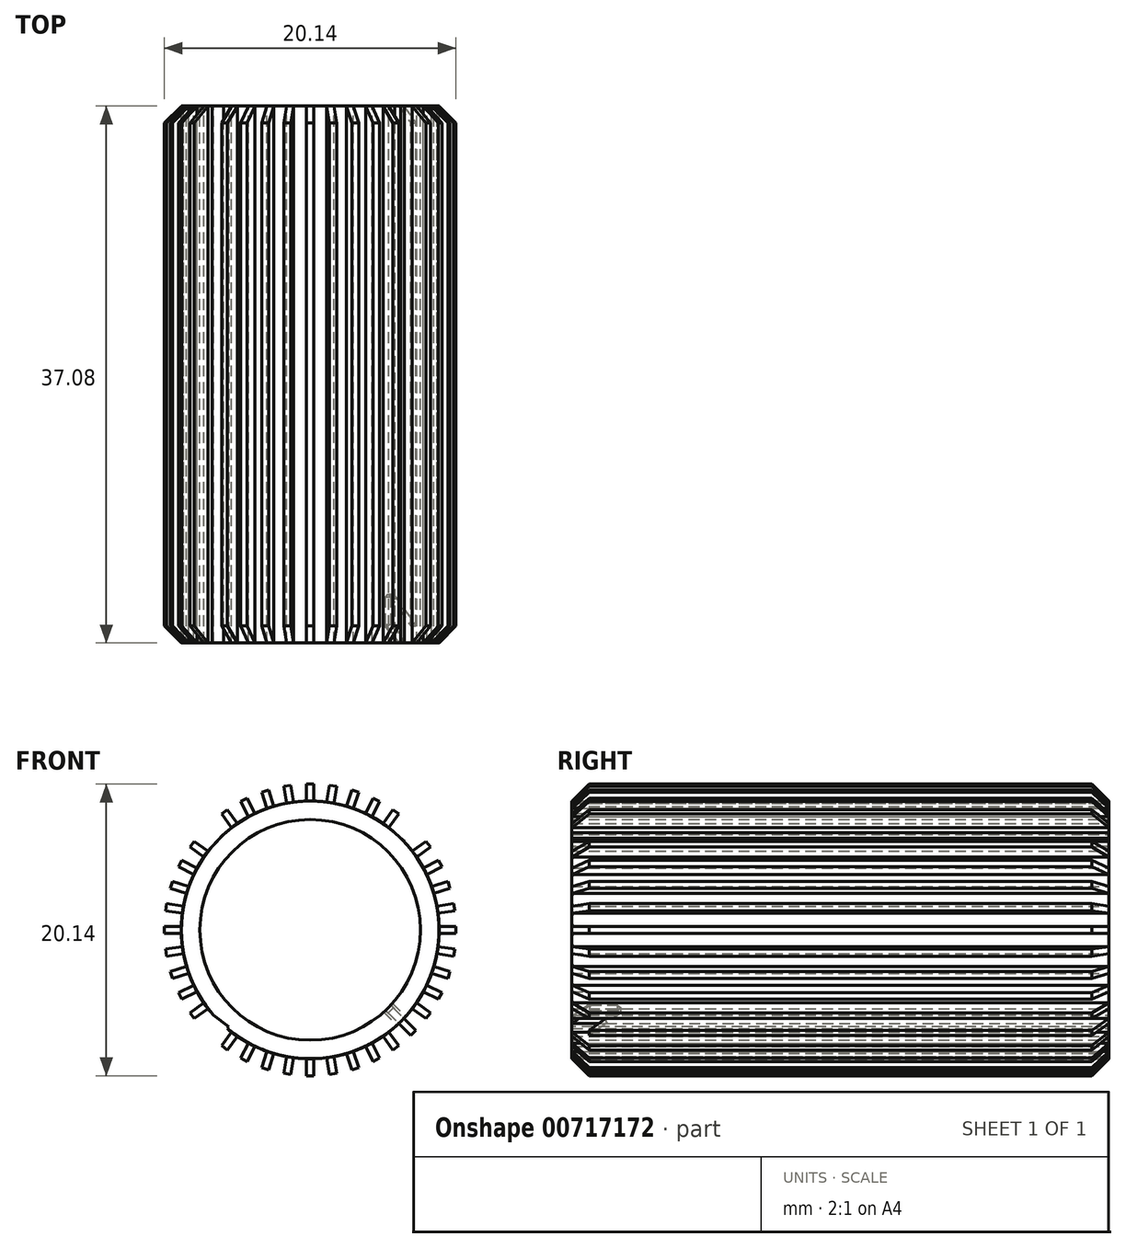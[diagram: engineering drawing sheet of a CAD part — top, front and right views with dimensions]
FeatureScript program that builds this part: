
annotation { "Feature Type Name" : "Feature", "Feature Type Description" : "" }
export const myFeature = defineFeature(function(context is Context, id is Id, definition is map)
    precondition{}
    {
        {
            var Q0;
            Q0=qCreatedBy(makeId("Front.planeOp"),FACE);
            var sketch = newSketch(context, id + "F0", { "sketchPlane" : qUnion([Q0])});
            skCircle(sketch, "E0", {"center": v(0, 0) * mm, "radius": 7.62 * mm});
            skCircle(sketch, "E1", {"center": v(0, 0) * mm, "radius": 8.9 * mm});
            skLineSegment(sketch, "E2.bottom", {"start": v(-0.25, 10.07) * mm, "end": v(0.25, 10.07) * mm});
            skLineSegment(sketch, "E2.left", {"start": v(-0.25, 10.07) * mm, "end": v(-0.25, 8.89) * mm});
            skLineSegment(sketch, "E2.right", {"start": v(0.25, 10.07) * mm, "end": v(0.25, 8.89) * mm});
            skSolve(sketch);
        }
        {
            var Q0;
            Q0 = qSketchRegion(id + "F0", true);
            extrude(context, id + "F1", {"entities" : qUnion([Q0]), "endBound" : BoundingType.SYMMETRIC, "depth" : 37.08 * mm, "offsetDistance" : 25.4 * mm});
        }
        {
            var Q0;
            Q0=qCreatedBy(makeId("Right.planeOp"),FACE);
            var sketch = newSketch(context, id + "F2", { "sketchPlane" : qUnion([Q0])});
            skLineSegment(sketch, "E3", {"start": v(-18.54, 8.89) * mm, "end": v(-17.09, 10.34) * mm});
            skLineSegment(sketch, "E4", {"start": v(-17.09, 10.34) * mm, "end": v(-18.74, 10.34) * mm});
            skLineSegment(sketch, "E5", {"start": v(-18.74, 10.34) * mm, "end": v(-18.54, 8.89) * mm});
            skLineSegment(sketch, "E6", {"start": v(0, 0) * mm, "end": v(0, 13.72) * mm, "construction": true});
            skLineSegment(sketch, "E7.MirrorCS", {"start": v(18.54, 8.89) * mm, "end": v(17.09, 10.34) * mm});
            skLineSegment(sketch, "E8.MirrorCS", {"start": v(17.09, 10.34) * mm, "end": v(18.74, 10.34) * mm});
            skLineSegment(sketch, "E9.MirrorCS", {"start": v(18.74, 10.34) * mm, "end": v(18.54, 8.89) * mm});
            skSolve(sketch);
        }
        {
            var Q0;
            Q0 = qSketchRegion(id + "F2", true);
            extrude(context, id + "F3", {"entities" : qUnion([Q0]), "operationType" : NewBodyOperationType.REMOVE, "endBound" : BoundingType.SYMMETRIC, "oppositeDirection" : true, "depth" : 25.4 * mm, "offsetDistance" : 25.4 * mm});
        }
        {
            var Q0;
            Q0=makeQuery(id+"F1.opExtrude","SWEPT_BODY",BODY,{"disambiguationData":[OSD([sQuery(id+"F0.wireOp",EDGE,"E0"),sQuery(id+"F0.wireOp",EDGE,"E1"),sQuery(id+"F0.wireOp",EDGE,"E2.bottom"),sQuery(id+"F0.wireOp",EDGE,"E2.left"),sQuery(id+"F0.wireOp",EDGE,"E2.right")])]});
            var Q1;
            Q1=makeQuery(id+"F1.opExtrude","CAP_EDGE",EDGE,{"disambiguationData":[OSD([sQuery(id+"F0.wireOp",EDGE,"E0")])],"isStart":false});
            circularPattern(context, id + "F4", {"entities" : qUnion([Q0]), "axis" : qUnion([Q1]), "angle" : 360 * degree, "instanceCount" : 40, "equalSpace" : true});
        }
        {
            var Q0;
            Q0=qCreatedBy(makeId("Front.planeOp"),FACE);
            var sketch = newSketch(context, id + "F5", { "sketchPlane" : qUnion([Q0])});
            skLineSegment(sketch, "E10", {"start": v(-10.71, 10.34) * mm, "end": v(10.44, -9.9) * mm, "construction": true});
            skLineSegment(sketch, "E11", {"start": v(9.39, 9.65) * mm, "end": v(-8.3, -8.84) * mm, "construction": true});
            skLineSegment(sketch, "E12", {"start": v(-8.28, 7.14) * mm, "end": v(-7.33, 8.13) * mm});
            skLineSegment(sketch, "E13", {"start": v(-7.33, 8.13) * mm, "end": v(-5.86, 6.72) * mm});
            skLineSegment(sketch, "E14", {"start": v(-5.86, 6.72) * mm, "end": v(-6.78, 5.75) * mm});
            skLineSegment(sketch, "E15", {"start": v(-6.78, 5.75) * mm, "end": v(-8.28, 7.14) * mm});
            skLineSegment(sketch, "E16", {"start": v(5.82, 6.72) * mm, "end": v(7.24, 8.2) * mm});
            skLineSegment(sketch, "E17", {"start": v(7.24, 8.2) * mm, "end": v(8.12, 7.36) * mm});
            skLineSegment(sketch, "E18", {"start": v(8.12, 7.36) * mm, "end": v(6.73, 5.91) * mm});
            skLineSegment(sketch, "E19", {"start": v(6.73, 5.91) * mm, "end": v(5.82, 6.72) * mm});
            skLineSegment(sketch, "E20", {"start": v(-6.69, -5.88) * mm, "end": v(-7.95, -7.2) * mm});
            skLineSegment(sketch, "E21", {"start": v(-8.03, -7.12) * mm, "end": v(-6.98, -8.12) * mm});
            skLineSegment(sketch, "E22", {"start": v(-6.98, -8.12) * mm, "end": v(-5.62, -6.69) * mm});
            skLineSegment(sketch, "E23", {"start": v(-5.62, -6.69) * mm, "end": v(-6.69, -5.88) * mm});
            skLineSegment(sketch, "E24", {"start": v(5.82, -6.72) * mm, "end": v(7.34, -8.18) * mm});
            skLineSegment(sketch, "E25", {"start": v(7.28, -8.04) * mm, "end": v(8.33, -6.95) * mm});
            skLineSegment(sketch, "E26", {"start": v(8.33, -6.95) * mm, "end": v(6.76, -5.77) * mm});
            skSolve(sketch);
        }
        {
            var Q0;
            Q0 = qSketchRegion(id + "F5", true);
            extrude(context, id + "F6", {"entities" : qUnion([Q0]), "operationType" : NewBodyOperationType.REMOVE, "endBound" : BoundingType.SYMMETRIC, "oppositeDirection" : true, "depth" : 41.66 * mm, "offsetDistance" : 25.4 * mm});
        }
        {
            var Q0;
            Q0=makeQuery(id+"F4.opPattern","COPY",FACE,{"derivedFrom":makeQuery(id+"F3.boolean.opBoolean","COPY",FACE,{"derivedFrom":makeQuery(id+"F3.opExtrude","SWEPT_FACE",FACE,{"disambiguationData":[OSD([sQuery(id+"F2.wireOp",EDGE,"E3")])]})}),"instanceName":"25"});
            extrude(context, id + "F7", {"entities" : qUnion([Q0]), "operationType" : NewBodyOperationType.REMOVE, "oppositeDirection" : true, "depth" : 3.12 * mm, "offsetDistance" : 25.4 * mm});
        }
    });
